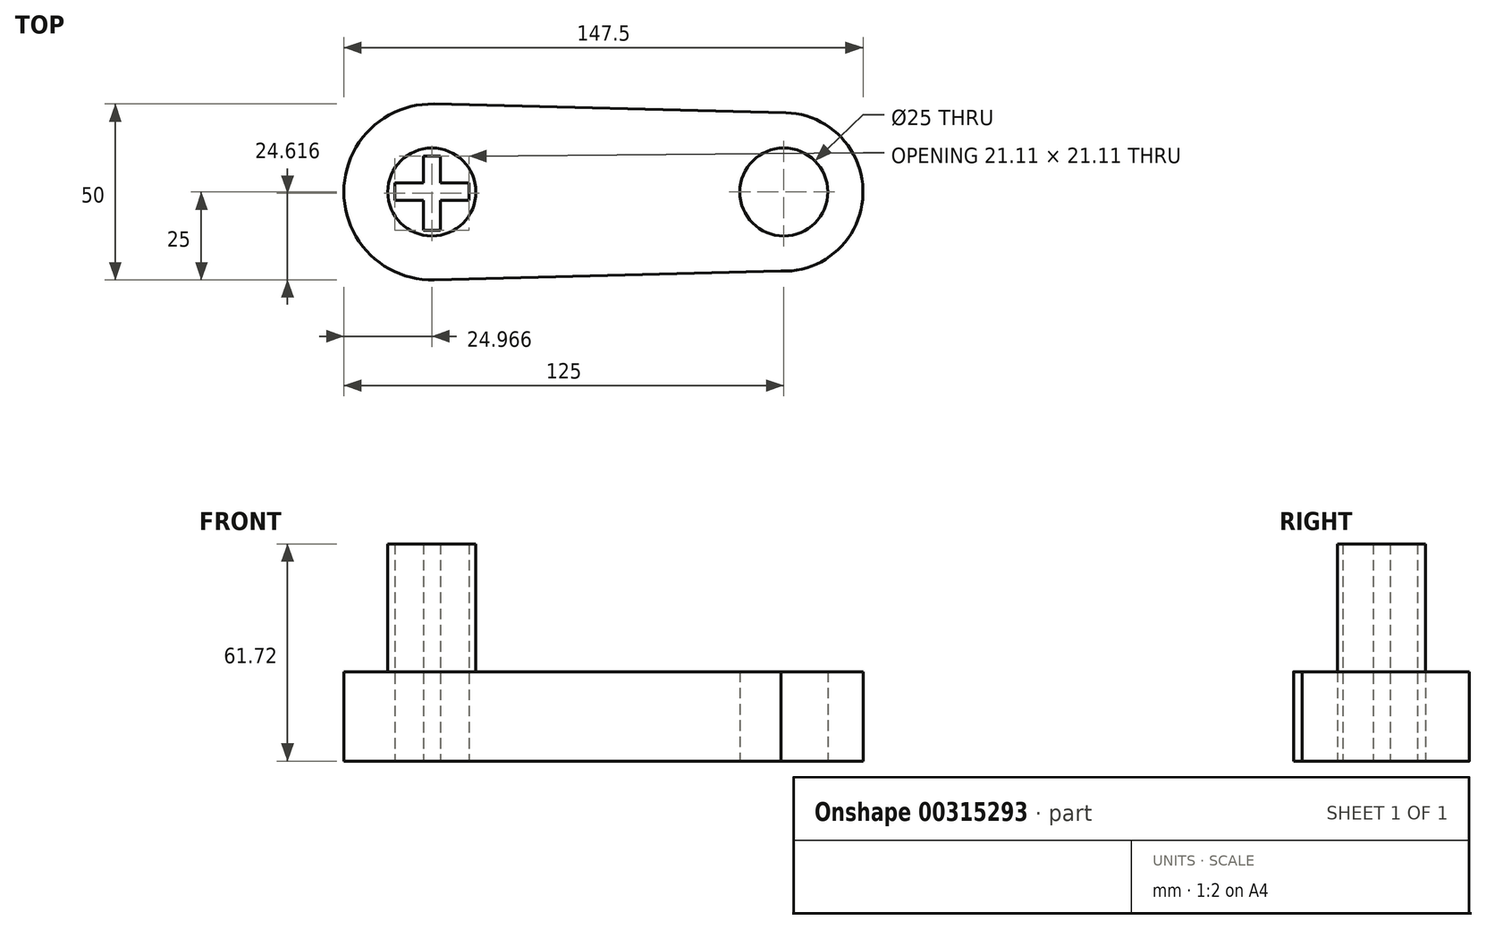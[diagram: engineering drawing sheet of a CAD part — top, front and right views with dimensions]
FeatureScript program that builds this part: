
annotation { "Feature Type Name" : "Feature", "Feature Type Description" : "" }
export const myFeature = defineFeature(function(context is Context, id is Id, definition is map)
    precondition{}
    {
        {
            var Q0;
            Q0=qCreatedBy(makeId("Top.planeOp"),FACE);
            var sketch = newSketch(context, id + "F0", { "sketchPlane" : qUnion([Q0])});
            skCircle(sketch, "E0", {"center": v(0, 0) * mm, "radius": 25 * mm});
            skCircle(sketch, "E1", {"center": v(100, 0) * mm, "radius": 22.5 * mm});
            skLineSegment(sketch, "E2", {"start": v(100.56, 22.5) * mm, "end": v(0, 25) * mm});
            skLineSegment(sketch, "E3", {"start": v(99.2, -22.49) * mm, "end": v(0, -25) * mm});
            skCircle(sketch, "E4", {"center": v(0, 0) * mm, "radius": 12.5 * mm});
            skCircle(sketch, "E5", {"center": v(100, 0) * mm, "radius": 12.5 * mm});
            skLineSegment(sketch, "E6.bottom", {"start": v(-2.44, 10.17) * mm, "end": v(2.43, 10.17) * mm});
            skLineSegment(sketch, "E6.top", {"start": v(-2.44, -10.94) * mm, "end": v(2.43, -10.94) * mm});
            skLineSegment(sketch, "E6.left", {"start": v(-2.44, 10.17) * mm, "end": v(-2.44, -10.94) * mm});
            skLineSegment(sketch, "E6.right", {"start": v(2.43, 10.17) * mm, "end": v(2.43, -10.94) * mm});
            skLineSegment(sketch, "E7.bottom", {"start": v(-10.59, 2.53) * mm, "end": v(10.52, 2.53) * mm});
            skLineSegment(sketch, "E7.top", {"start": v(-10.59, -2.35) * mm, "end": v(10.52, -2.35) * mm});
            skLineSegment(sketch, "E7.left", {"start": v(-10.59, 2.53) * mm, "end": v(-10.59, -2.35) * mm});
            skLineSegment(sketch, "E7.right", {"start": v(10.52, 2.53) * mm, "end": v(10.52, -2.35) * mm});
            skSolve(sketch);
        }
        {
            var Q0;
            Q0 = qSketchRegion(id + "F0", true);
            extrude(context, id + "F1", {"entities" : qUnion([Q0]), "depth" : 25.4 * mm});
        }
        {
            var Q0;
            {var subQ1=sQuery(id+"F0.wireOp",EDGE,"E6.bottom");Q0=makeQuery(id+"F0.imprint","IMPRINT",FACE,{"disambiguationData":[TD([[makeQuery(id+"F0.imprint","IMPRINT",EDGE,{"derivedFrom":subQ1}),1.0]])]});}
            extrude(context, id + "F2", {"entities" : qUnion([Q0]), "operationType" : NewBodyOperationType.ADD, "depth" : 61.72 * mm});
        }
    });
